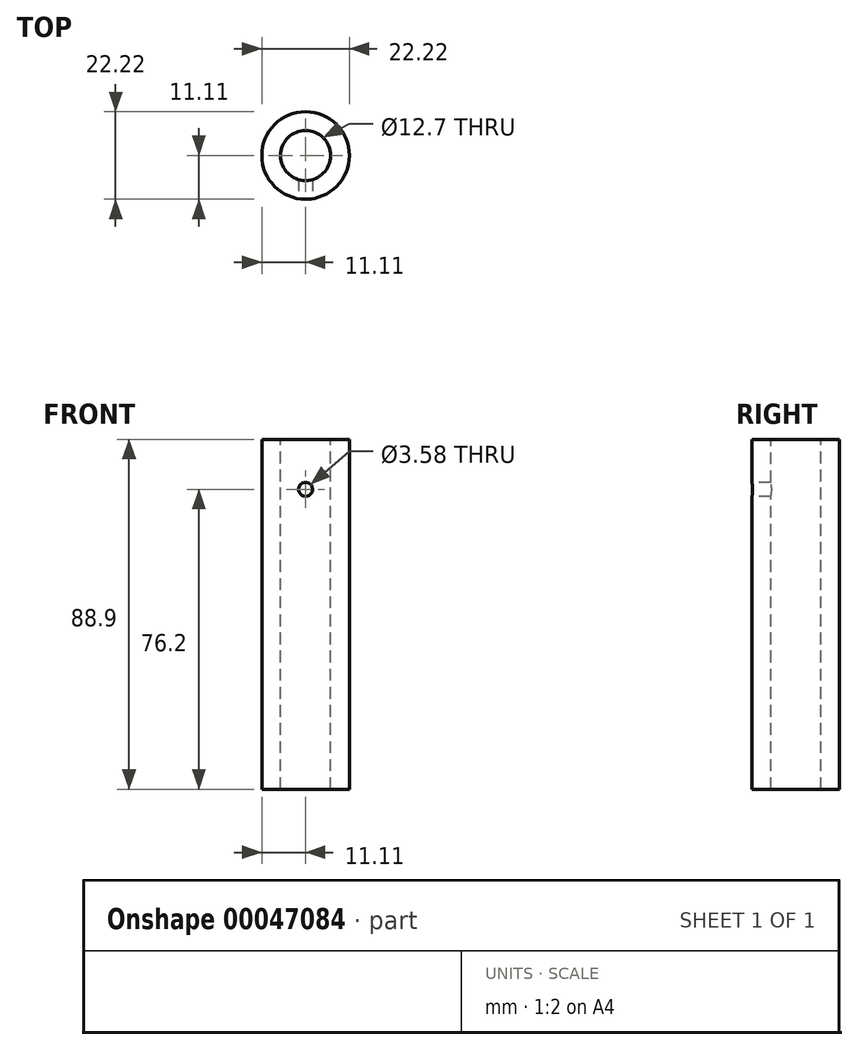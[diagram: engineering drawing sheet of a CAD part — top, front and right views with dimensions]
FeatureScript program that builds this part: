
annotation { "Feature Type Name" : "Feature", "Feature Type Description" : "" }
export const myFeature = defineFeature(function(context is Context, id is Id, definition is map)
    precondition{}
    {
        {
            var Q0;
            Q0=qCreatedBy(makeId("Top.planeOp"),FACE);
            var sketch = newSketch(context, id + "F0", { "sketchPlane" : qUnion([Q0])});
            skCircle(sketch, "E0", {"center": v(0, 0) * mm, "radius": 11.11 * mm});
            skSolve(sketch);
        }
        {
            var Q0;
            Q0=makeQuery(id+"F0.imprint","IMPRINT",FACE,{"disambiguationData":[TD([[makeQuery(id+"F0.imprint","IMPRINT",EDGE,{"derivedFrom":sQuery(id+"F0.wireOp",EDGE,"E0")}),1.0]])]});
            extrude(context, id + "F1", {"entities" : qUnion([Q0]), "endBound" : BoundingType.SYMMETRIC, "depth" : 88.9 * mm});
        }
        {
            var Q0;
            Q0=makeQuery(id+"F1.opExtrude","CAP_FACE",FACE,{"disambiguationData":[OSD([sQuery(id+"F0.wireOp",EDGE,"E0")])],"isStart":false});
            var sketch = newSketch(context, id + "F2", { "sketchPlane" : qUnion([Q0])});
            skCircle(sketch, "E1", {"center": v(0, 0) * mm, "radius": 6.35 * mm});
            skSolve(sketch);
        }
        {
            var Q0;
            Q0 = qSketchRegion(id + "F2", true);
            var Q1;
            Q1=makeQuery(id+"F1.opExtrude","CAP_FACE",FACE,{"disambiguationData":[OSD([sQuery(id+"F0.wireOp",EDGE,"E0")])],"isStart":true});
            extrude(context, id + "F3", {"entities" : qUnion([Q0]), "operationType" : NewBodyOperationType.REMOVE, "endBound" : BoundingType.UP_TO_SURFACE, "oppositeDirection" : true, "endBoundEntityFace" : qUnion([Q1]), "depth" : 25.4 * mm});
        }
        {
            var Q0;
            Q0=qCreatedBy(makeId("Front.planeOp"),FACE);
            cPlane(context, id + "F4", {"entities" : qUnion([Q0]), "cplaneType" : CPlaneType.OFFSET, "offset" : 11.1 * mm, "width" : 152.4 * mm, "height" : 152.4 * mm});
        }
        {
            var Q0;
            Q0=qCreatedBy(id+"F4.planeOp",FACE);
            var sketch = newSketch(context, id + "F5", { "sketchPlane" : qUnion([Q0])});
            skCircle(sketch, "E2", {"center": v(0, 31.75) * mm, "radius": 1.8 * mm});
            skCircle(sketch, "E3.MirrorC", {"center": v(0, -31.75) * mm, "radius": 1.8 * mm});
            skSolve(sketch);
        }
        {
            var Q0;
            Q0=makeQuery(id+"F5.imprint","IMPRINT",FACE,{"disambiguationData":[TD([[makeQuery(id+"F5.imprint","IMPRINT",EDGE,{"derivedFrom":sQuery(id+"F5.wireOp",EDGE,"E3.MirrorC")}),-1.0]])]});
            var Q1;
            Q1=makeQuery(id+"F5.imprint","IMPRINT",FACE,{"disambiguationData":[TD([[makeQuery(id+"F5.imprint","IMPRINT",EDGE,{"derivedFrom":sQuery(id+"F5.wireOp",EDGE,"E2")}),1.0]])]});
            var Q2;
            Q2=makeQuery(id+"F1.opExtrude","SWEPT_FACE",FACE,{"disambiguationData":[OSD([sQuery(id+"F0.wireOp",EDGE,"E0")])]});
            extrude(context, id + "F6", {"entities" : qUnion([Q0, Q1]), "operationType" : NewBodyOperationType.REMOVE, "endBound" : BoundingType.UP_TO_NEXT, "oppositeDirection" : true, "endBoundEntityFace" : qUnion([Q2]), "depth" : 25.4 * mm});
        }
    });
